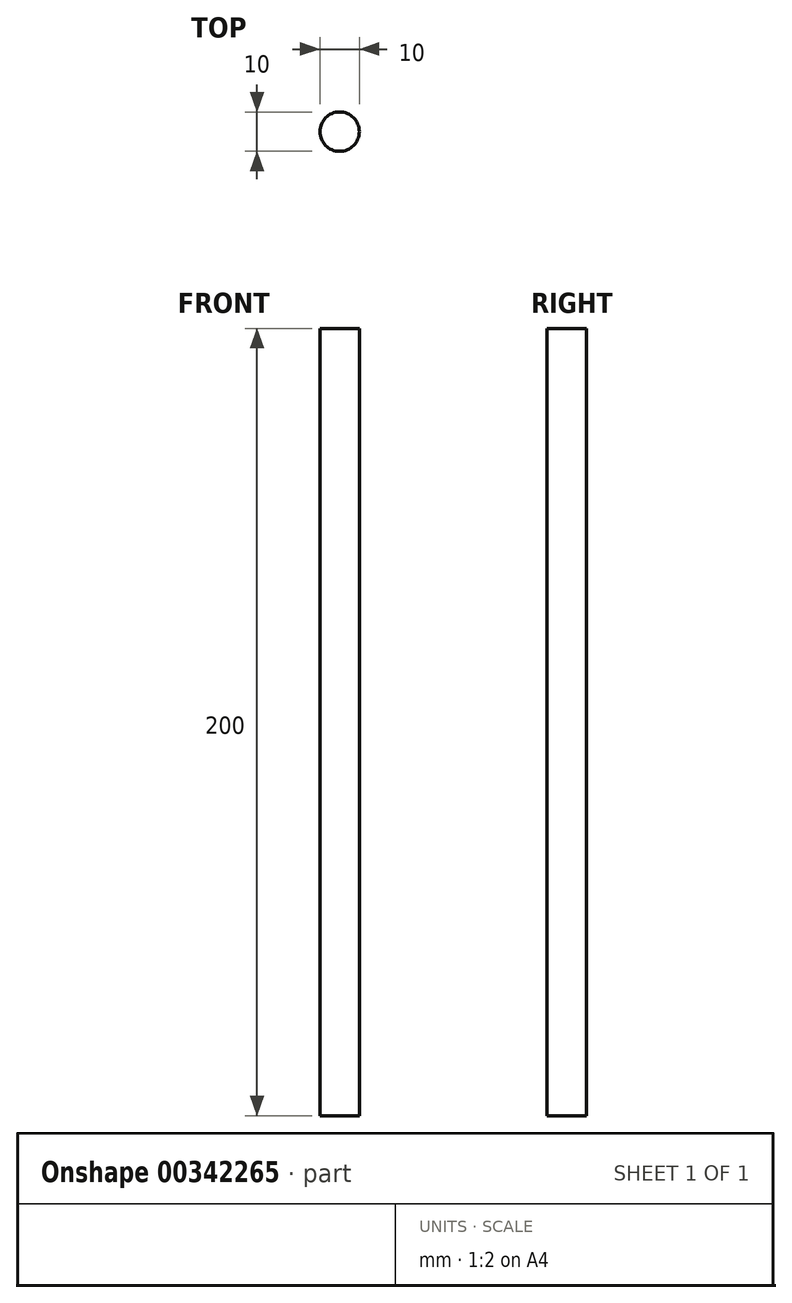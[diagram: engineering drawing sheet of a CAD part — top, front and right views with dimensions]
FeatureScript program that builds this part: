
annotation { "Feature Type Name" : "Feature", "Feature Type Description" : "" }
export const myFeature = defineFeature(function(context is Context, id is Id, definition is map)
    precondition{}
    {
        {
            var Q0;
            Q0=qCreatedBy(makeId("Top.planeOp"),FACE);
            var sketch = newSketch(context, id + "F0", { "sketchPlane" : qUnion([Q0])});
            skCircle(sketch, "E0", {"center": v(-36.25, -26.2) * mm, "radius": 5 * mm});
            skSolve(sketch);
        }
        {
            var Q0;
            Q0 = qSketchRegion(id + "F0", true);
            extrude(context, id + "F1", {"entities" : qUnion([Q0]), "depth" : 200 * mm});
        }
    });
